# Revit family: NLRS_33_RB_DO_BILCO_dakluik_L-50TB
name_source: partatom
category: Doors
revit_build: Autodesk Revit 2015 (Build: 20140223_1515(x64)
units: mm (PartAtom-declared; Revit-internal decimal feet)

## types (1)
- NLRS_33_RB_DO_BILCO_dakluik_L-50TB
    Description = standaard aluminium dakluik
    HandlePosition = 820 mm  [stored 2.69029 ft]
    Height = 405 mm  [stored 1.32874 ft]
    Length = 2720 mm
    Manufacturer = Bilco
    RWA = No
    Rough Height = 0 mm  [stored 0 ft]
    Rough Width = 0 mm  [stored 0 ft]
    Thickness = 0 mm  [stored 0 ft]
    Width = 1040 mm
    bediening = handmatig
    belasting = 195.00 kg/m²
    brandwerend 120 min = No
    brandwerend 30 min = No
    brandwerend 60 min = No
    brandwerend 90 min = No
    breedte = 1040 mm
    breedte_paneel = 950 mm
    cilinderslot = Yes
    code productgroep = LUI
    conservering = brut
    dagmaatbreedte = 760 mm  [stored 2.49344 ft]
    dagmaatlengte = 2440 mm  [stored 8.00525 ft]
    deurblad = vlak
    dikte_isolatie = 75 mm
    false = No
    geluidsreductie (dB) = 25
    gewicht (kg) = 138
    hoogte = 405 mm  [stored 1.32874 ft]
    hoogte_aandrijving = 323 mm  [stored 1.05971 ft]
    hoogte_opstand = 305 mm
    isolatie = Yes
    isolatiewaarde = 3.5900 (m²·K)/W
    lengte = 2720 mm
    lengte_paneel = 2630 mm
    loopslot = Yes
    materiaal = bcb_aluminium
    materiaal_secundair = <By Category>
    omranding dakopstand = Yes
    omranding hoekprofiel = No
    omranding waterafvoerend = No
    omschrijving = standaard aluminium dakluik
    openingshoek = 90.00°
    openstand vergrendeling = Yes
    plaatdikte = 2 mm  [stored 0.00656168 ft]
    productgroep = dakluiken
    scharnierend = Yes
    thermische onderbreking = Yes
    true = Yes
    veersysteem = Yes
    waterdicht = Yes

note: [stored X ft] marks values corroborated as IEEE doubles in the binary element streams (Revit-internal decimal feet)

## geometry (parser evidence)
native form markers: Blend x1604, Sweep x15
no freeform markers — native parametric forms only
